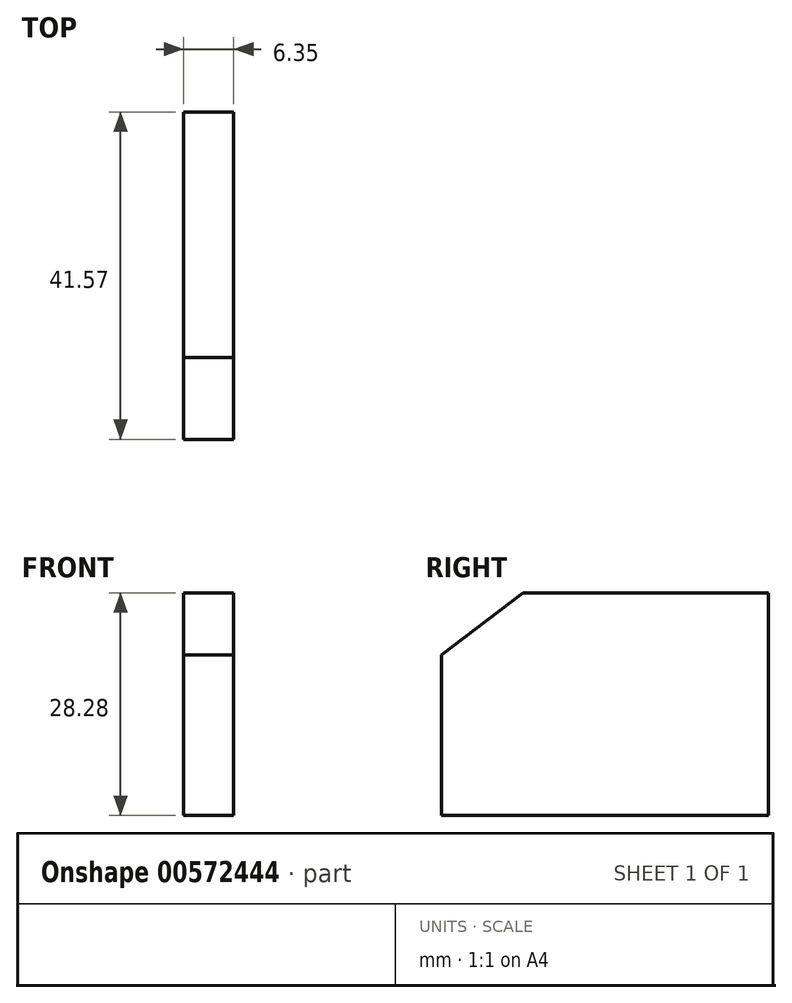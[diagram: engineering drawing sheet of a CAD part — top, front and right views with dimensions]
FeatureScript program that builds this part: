
annotation { "Feature Type Name" : "Feature", "Feature Type Description" : "" }
export const myFeature = defineFeature(function(context is Context, id is Id, definition is map)
    precondition{}
    {
        {
            var Q0;
            Q0=qCreatedBy(makeId("Right.planeOp"),FACE);
            var sketch = newSketch(context, id + "F0", { "sketchPlane" : qUnion([Q0])});
            skLineSegment(sketch, "E0", {"start": v(0, 0) * mm, "end": v(0, 20.36) * mm});
            skLineSegment(sketch, "E1", {"start": v(0, 20.36) * mm, "end": v(10.38, 28.28) * mm});
            skLineSegment(sketch, "E2", {"start": v(10.38, 28.28) * mm, "end": v(41.57, 28.28) * mm});
            skLineSegment(sketch, "E3", {"start": v(41.57, 28.28) * mm, "end": v(41.57, 0) * mm});
            skLineSegment(sketch, "E4", {"start": v(41.57, 0) * mm, "end": v(0, 0) * mm});
            skSolve(sketch);
        }
        {
            var Q0;
            Q0 = qSketchRegion(id + "F0", true);
            extrude(context, id + "F1", {"entities" : qUnion([Q0]), "depth" : 6.35 * mm, "offsetDistance" : 25.4 * mm});
        }
    });
